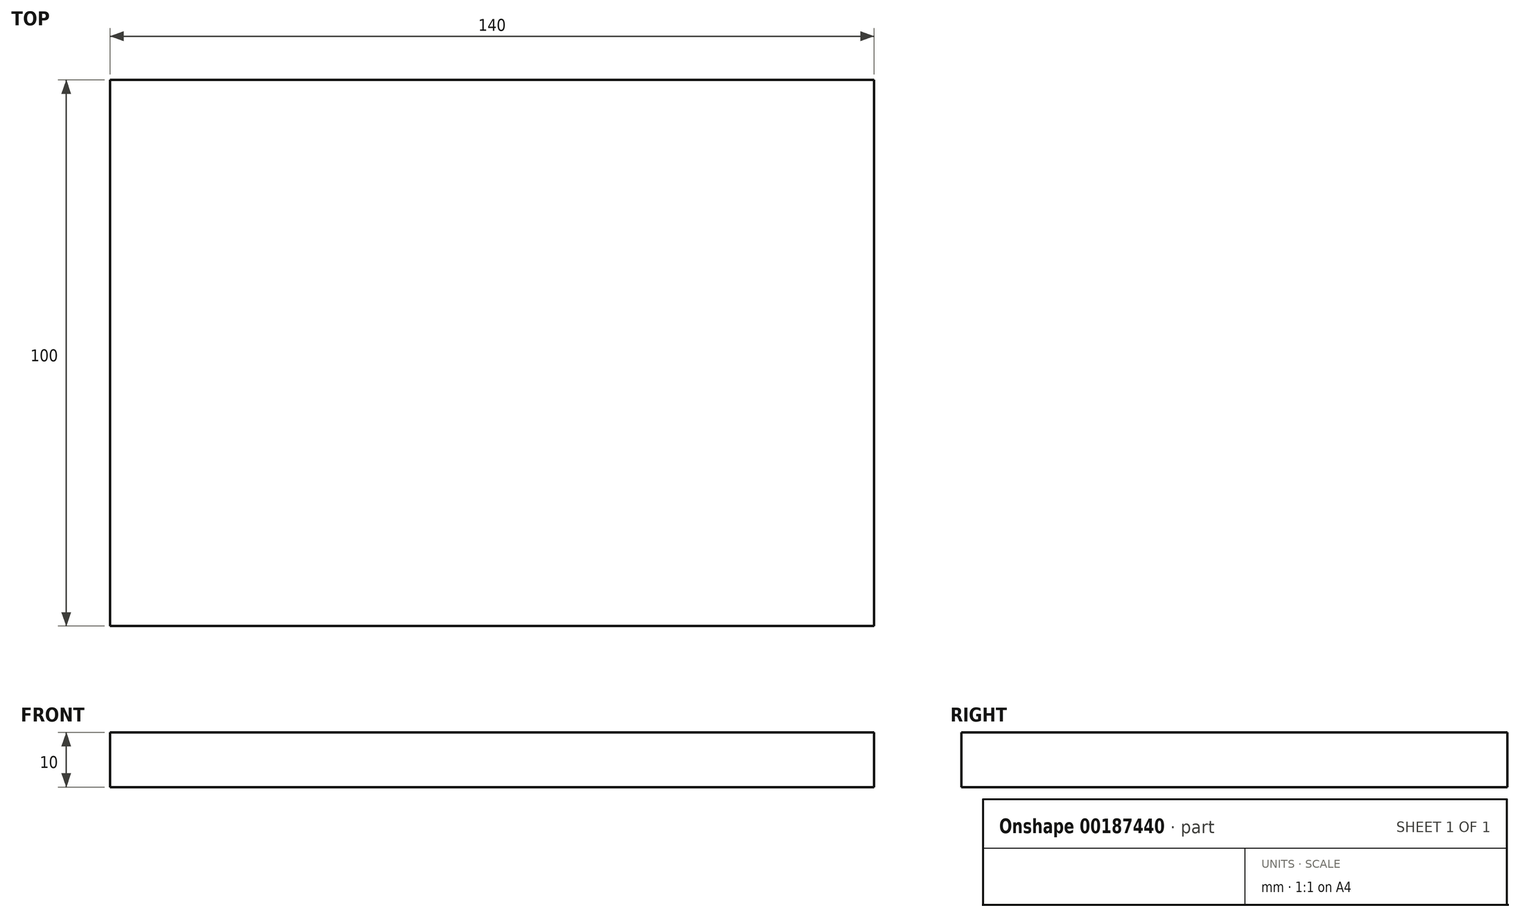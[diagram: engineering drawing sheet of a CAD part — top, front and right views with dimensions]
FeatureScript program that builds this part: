
annotation { "Feature Type Name" : "Feature", "Feature Type Description" : "" }
export const myFeature = defineFeature(function(context is Context, id is Id, definition is map)
    precondition{}
    {
        {
            var Q0;
            Q0=qCreatedBy(makeId("Right.planeOp"),FACE);
            var sketch = newSketch(context, id + "F0", { "sketchPlane" : qUnion([Q0])});
            skLineSegment(sketch, "E0.bottom", {"start": v(0, 0) * mm, "end": v(100, 0) * mm});
            skLineSegment(sketch, "E0.top", {"start": v(0, 10) * mm, "end": v(100, 10) * mm});
            skLineSegment(sketch, "E0.left", {"start": v(0, 0) * mm, "end": v(0, 10) * mm});
            skLineSegment(sketch, "E0.right", {"start": v(100, 0) * mm, "end": v(100, 10) * mm});
            skSolve(sketch);
        }
        {
            var Q0;
            Q0 = qSketchRegion(id + "F0", true);
            extrude(context, id + "F1", {"entities" : qUnion([Q0]), "depth" : 140 * mm});
        }
    });
